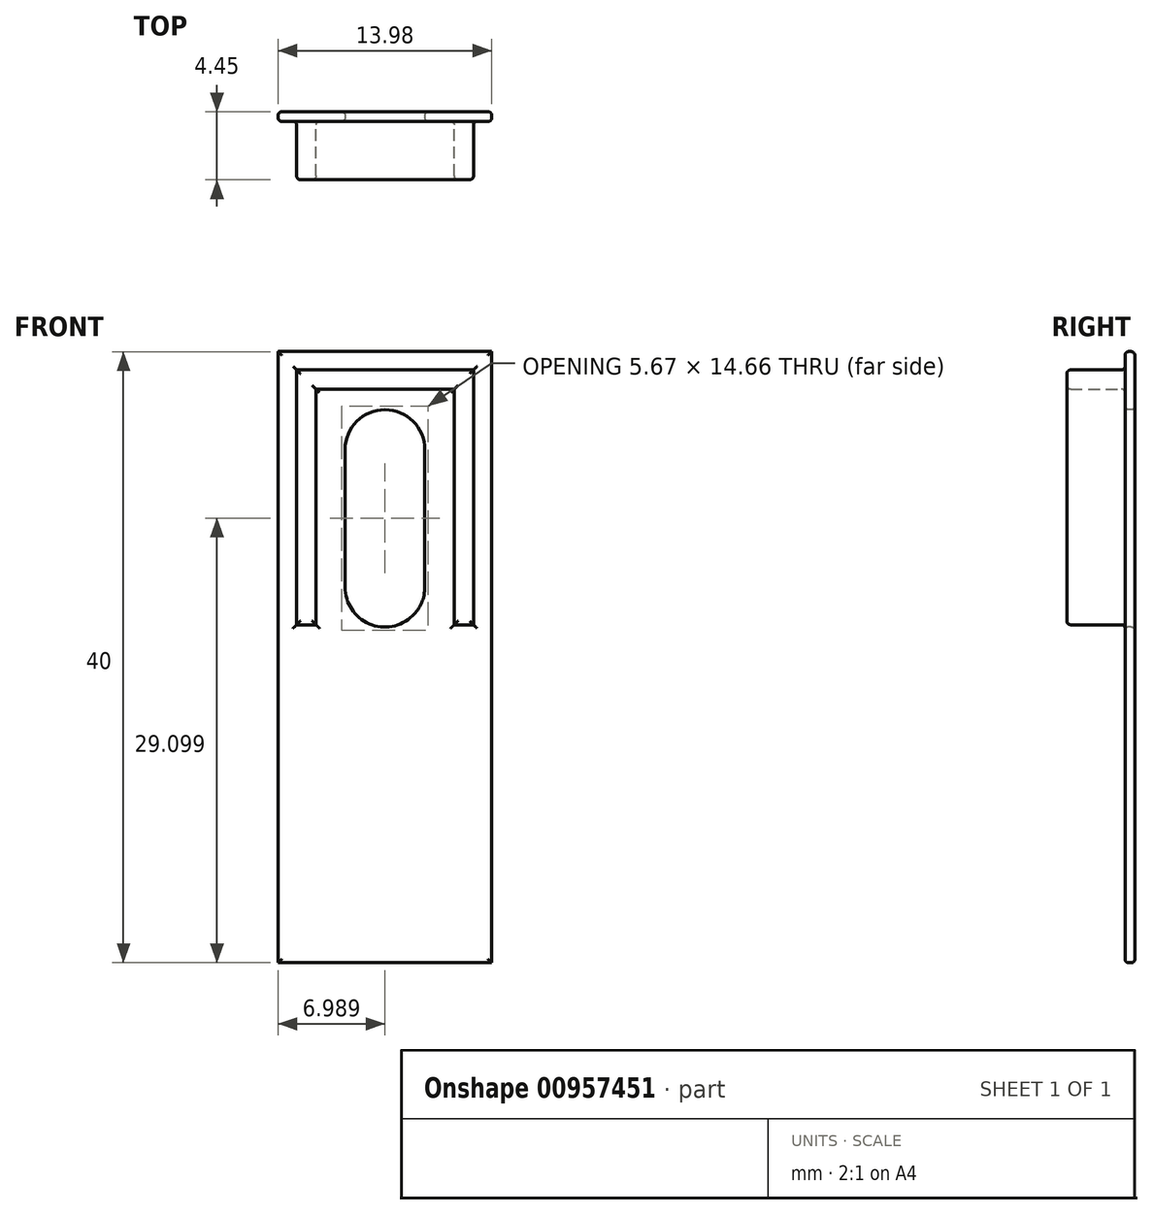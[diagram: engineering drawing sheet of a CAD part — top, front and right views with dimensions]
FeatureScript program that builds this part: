
annotation { "Feature Type Name" : "Feature", "Feature Type Description" : "" }
export const myFeature = defineFeature(function(context is Context, id is Id, definition is map)
    precondition{}
    {
        {
            var Q0;
            Q0=qCreatedBy(makeId("Front.planeOp"),FACE);
            var sketch = newSketch(context, id + "F0", { "sketchPlane" : qUnion([Q0])});
            skLineSegment(sketch, "E0.bottom", {"start": v(6.99, 20) * mm, "end": v(-6.98, 20) * mm});
            skLineSegment(sketch, "E0.top", {"start": v(6.98, -20) * mm, "end": v(-6.99, -20) * mm});
            skPoint(sketch, "E0.middle", {"position": v(0, 0) * mm});
            skLineSegment(sketch, "E1", {"start": v(6.99, 20) * mm, "end": v(6.98, -20) * mm});
            skLineSegment(sketch, "E2", {"start": v(-6.98, 20) * mm, "end": v(-6.99, -20) * mm});
            skSolve(sketch);
        }
        {
            var Q0;
            Q0=makeQuery(id+"F0.imprint","IMPRINT",FACE,{"disambiguationData":[TD([[makeQuery(id+"F0.imprint","IMPRINT",EDGE,{"derivedFrom":sQuery(id+"F0.wireOp",EDGE,"E0.bottom")}),1.0]])]});
            extrude(context, id + "F1", {"entities" : qUnion([Q0]), "depth" : 3.17 * mm, "offsetDistance" : 25.4 * mm});
        }
        {
            var Q0;
            Q0=makeQuery(id+"F1.opExtrude","CAP_FACE",FACE,{"disambiguationData":[OSD([sQuery(id+"F0.wireOp",EDGE,"E0.bottom"),sQuery(id+"F0.wireOp",EDGE,"E0.top"),sQuery(id+"F0.wireOp",EDGE,"E1"),sQuery(id+"F0.wireOp",EDGE,"E2")])],"isStart":true});
            extrude(context, id + "F2", {"entities" : qUnion([Q0]), "operationType" : NewBodyOperationType.REMOVE, "oppositeDirection" : true, "depth" : 2.54 * mm, "offsetDistance" : 25.4 * mm});
        }
        {
            var Q0;
            Q0=makeQuery(id+"F1.opExtrude","CAP_FACE",FACE,{"disambiguationData":[OSD([sQuery(id+"F0.wireOp",EDGE,"E0.bottom"),sQuery(id+"F0.wireOp",EDGE,"E0.top"),sQuery(id+"F0.wireOp",EDGE,"E1"),sQuery(id+"F0.wireOp",EDGE,"E2")])],"isStart":false});
            var sketch = newSketch(context, id + "F3", { "sketchPlane" : qUnion([Q0])});
            skArc(sketch, "E3.0", {"start": v(2.6, 13.6) * mm, "mid": v(1.84, 15.44) * mm, "end": v(0, 16.2) * mm});
            skLineSegment(sketch, "E3.1", {"start": v(-2.6, 13.6) * mm, "end": v(-2.6, 4.59) * mm});
            skArc(sketch, "E3.2", {"start": v(-2.6, 4.59) * mm, "mid": v(-1.02, 2.19) * mm, "end": v(1.8, 2.7) * mm});
            skArc(sketch, "E3.3", {"start": v(0, 16.2) * mm, "mid": v(-1.84, 15.44) * mm, "end": v(-2.6, 13.6) * mm});
            skArc(sketch, "E3.4", {"start": v(1.8, 2.7) * mm, "mid": v(2.4, 3.56) * mm, "end": v(2.6, 4.58) * mm});
            skLineSegment(sketch, "E3.5", {"start": v(2.6, 4.58) * mm, "end": v(2.6, 13.6) * mm});
            skLineSegment(sketch, "E4", {"start": v(0, 1.98) * mm, "end": v(0, 16.2) * mm});
            skSolve(sketch);
        }
        {
            var Q0;
            Q0=makeQuery(id+"F1.opExtrude","CAP_FACE",FACE,{"disambiguationData":[OSD([sQuery(id+"F0.wireOp",EDGE,"E0.bottom"),sQuery(id+"F0.wireOp",EDGE,"E0.top"),sQuery(id+"F0.wireOp",EDGE,"E1"),sQuery(id+"F0.wireOp",EDGE,"E2")])],"isStart":false});
            var sketch = newSketch(context, id + "F4", { "sketchPlane" : qUnion([Q0])});
            skLineSegment(sketch, "E5", {"start": v(-4.51, 2.12) * mm, "end": v(-4.51, 17.54) * mm});
            skLineSegment(sketch, "E6.MirrorCS", {"start": v(4.53, 2.12) * mm, "end": v(4.53, 17.54) * mm});
            skLineSegment(sketch, "E7", {"start": v(-4.51, 17.54) * mm, "end": v(4.53, 17.54) * mm});
            skLineSegment(sketch, "E8", {"start": v(4.53, 2.12) * mm, "end": v(5.8, 2.12) * mm});
            skLineSegment(sketch, "E9", {"start": v(5.8, 2.12) * mm, "end": v(5.8, 18.8) * mm});
            skLineSegment(sketch, "E10", {"start": v(-4.51, 2.12) * mm, "end": v(-5.78, 2.12) * mm});
            skLineSegment(sketch, "E11", {"start": v(5.8, 18.8) * mm, "end": v(-5.78, 18.8) * mm});
            skLineSegment(sketch, "E12", {"start": v(-5.78, 18.8) * mm, "end": v(-5.78, 2.12) * mm});
            skLineSegment(sketch, "E13.top", {"start": v(-5.78, 18.8) * mm, "end": v(5.8, 18.8) * mm});
            skLineSegment(sketch, "E13.left", {"start": v(-5.78, 2.12) * mm, "end": v(-5.78, 18.8) * mm});
            skPoint(sketch, "E14", {"position": v(0, 10.46) * mm});
            skLineSegment(sketch, "E15.bottom", {"start": v(1.6, 12.8) * mm, "end": v(-1.6, 12.8) * mm});
            skLineSegment(sketch, "E15.top", {"start": v(1.6, 8.13) * mm, "end": v(-1.6, 8.13) * mm});
            skLineSegment(sketch, "E15.left", {"start": v(1.6, 12.8) * mm, "end": v(1.6, 8.13) * mm});
            skLineSegment(sketch, "E15.right", {"start": v(-1.6, 12.8) * mm, "end": v(-1.6, 8.13) * mm});
            skSolve(sketch);
        }
        {
            var Q0;
            Q0=makeQuery(id+"F3.imprint","IMPRINT",FACE,{"disambiguationData":[TD([[makeQuery(id+"F3.imprint","IMPRINT",EDGE,{"derivedFrom":sQuery(id+"F3.wireOp",EDGE,"E3.0")}),1.0]])]});
            var Q1;
            {var subQ0=sQuery(id+"F3.wireOp",EDGE,"E3.1");Q1=makeQuery(id+"F3.imprint","IMPRINT",FACE,{"disambiguationData":[TD([[makeQuery(id+"F3.imprint","IMPRINT",EDGE,{"derivedFrom":subQ0}),1.0]])]});}
            extrude(context, id + "F5", {"entities" : qUnion([Q0, Q1]), "operationType" : NewBodyOperationType.REMOVE, "oppositeDirection" : true, "depth" : 25.4 * mm, "offsetDistance" : 25.4 * mm});
        }
        {
            var Q0;
            Q0=makeQuery(id+"F4.imprint","IMPRINT",FACE,{"disambiguationData":[TD([[makeQuery(id+"F4.imprint","IMPRINT",EDGE,{"derivedFrom":sQuery(id+"F4.wireOp",EDGE,"E5")}),1.0]])]});
            extrude(context, id + "F6", {"entities" : qUnion([Q0]), "operationType" : NewBodyOperationType.ADD, "depth" : 3.8 * mm, "offsetDistance" : 25.4 * mm});
        }
        {
            var Q0;
            Q0=makeQuery(id+"F2.boolean.opBoolean","COPY",FACE,{"derivedFrom":makeQuery(id+"F2.opExtrude","CAP_FACE",FACE,{"disambiguationData":[OSD([sQuery(id+"F0.wireOp",EDGE,"E0.bottom"),sQuery(id+"F0.wireOp",EDGE,"E0.top"),sQuery(id+"F0.wireOp",EDGE,"E1"),sQuery(id+"F0.wireOp",EDGE,"E2")])],"isStart":false})});
            fillet(context, id + "F7", {"entities" : qUnion([Q0]), "radius" : 0.23 * mm, "tangentPropagation" : true, "allowEdgeOverflow" : false});
        }
        {
            var Q0;
            Q0=makeQuery(id+"F1.opExtrude","CAP_FACE",FACE,{"disambiguationData":[OSD([sQuery(id+"F0.wireOp",EDGE,"E0.bottom"),sQuery(id+"F0.wireOp",EDGE,"E0.top"),sQuery(id+"F0.wireOp",EDGE,"E1"),sQuery(id+"F0.wireOp",EDGE,"E2")])],"isStart":false});
            fillet(context, id + "F8", {"entities" : qUnion([Q0]), "radius" : 0.23 * mm, "tangentPropagation" : true, "allowEdgeOverflow" : false});
        }
        {
            var Q0;
            Q0=makeQuery(id+"F6.opExtrude","CAP_FACE",FACE,{"disambiguationData":[OSD([sQuery(id+"F4.wireOp",EDGE,"E5"),sQuery(id+"F4.wireOp",EDGE,"E6.MirrorCS"),sQuery(id+"F4.wireOp",EDGE,"E7"),sQuery(id+"F4.wireOp",EDGE,"E8"),sQuery(id+"F4.wireOp",EDGE,"E9"),sQuery(id+"F4.wireOp",EDGE,"E10"),sQuery(id+"F4.wireOp",EDGE,"E11"),sQuery(id+"F4.wireOp",EDGE,"E12")])],"isStart":false});
            fillet(context, id + "F9", {"entities" : qUnion([Q0]), "radius" : 0.25 * mm, "tangentPropagation" : true, "allowEdgeOverflow" : false});
        }
    });
